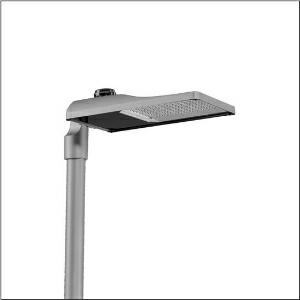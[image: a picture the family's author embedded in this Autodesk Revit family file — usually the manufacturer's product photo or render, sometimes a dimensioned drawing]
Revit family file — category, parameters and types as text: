
# Revit family: streetlight_sl_31_maxi___st1_5a_5xh8p7bn08sa_f059
name_source: partatom
category: Lighting Fixtures
units: mm (PartAtom-declared; Revit-internal decimal feet)

## family parameters
Cut with Voids When Loaded = No
Host = Face
Light Source = No
Part Type = Normal
Room Calculation Point = No
Round Connector Dimension = Use Diameter
Shared = No

## types (1)
- --- (1 x LED, 22010 lm, 208.6 W, 2200K)
    Apparent Load = 209 VA
    CIE Flux Codes = 22 53 95 100 100
    Color Rendering = 70
    Color Temperature = 2200K
    Default Elevation = 1800 mm
    Description = Streetlight SL 31 maxi NEMA (7pin) mast luminaire for post-top, side-entry; light control with lens of PMMA; light distribution: ST1.5a, direct asymmetric distribution, for standard-compliant lighting for roads and squares; LED: luminous flux: 22.010lm, light colour: 722, colour temperature: 2200K; luminous efficacy: 105,5lm/W; control: pre-setting: linear dimming characteristic, flexible luminous flux parameterisation, time-dependent luminous flux control, constant luminous flux control, intelligent temperature release in ECG and LED module, overheat protection; luminaire housing, of diecast aluminium, Siteco® metallic grey (DB 702S), corrosivity category C5 high according to DIN EN ISO 12944; cover of toughened safety glass, transparent, opened without tools; mast flange of diecast aluminium, Siteco® metallic grey (DB 702S), spigot size: 76/60mm, mast flange included unmounted; with cable H07RN-F 3x 1.5mm², cable length: 14,5m, connection cable pre-assembled; mains connection: 220..240V, AC, 50/60Hz; power consumption (at start of service life): 208,6W / (at end of service life): 233,1W / (with reduced operation 50%): 88W; protection rating (complete): IP66; insulation class (complete): insulation class I (protective earthing); impact resistance: IK10; certification: CE, ENEC, ENEC+, VDE, UKCA; permissible operating ambient temperature for outdoor applications: -40..+50°C; packaging unit: 1 piece

Light Distribution: ST1.5a
    Height = 79 mm
    Lamp = 1 x LED
    Lamp Light Flux = 22010 lm
    Lamp Power = 208.6 W
    Lamp count = 1
    Length = 657 mm
    Luminous efficacy = 106 lm/W
    Manufacturer = Siteco
    ModVariant = No
    Model = 5XH8P7BN08SA
    Number of Poles = 1
    OnlyDefault = Yes
    Power Factor = 1
    Product Name = Streetlight SL 31 maxi | ST1.5a
    Product group = mast luminaire | pylon top
    ProductGroupID = 6100
    Protection Class = Protection class I
    Protection Degree = IP 66
    RLX_Detail_Level = 1
    RLX_Emergency_Light_Flux = 0 lm
    RLX_Emergency_Type = 0
    RLX_Emergency_Type_DB = No
    RlxData = <blob elided: 30453 chars, md5=e5dbac57>
    Socket = socket
    Standby Power = 0 W
    System Light Flux = 22009 lm
    System Power = 209 W
    Type Comments = factory setting: luminous flux: 100 % | dim-lin: 254 | 718 mA
    Type Image = l_1300293.jpg
    URL = http://relux.com
    VarID = @adj_008253
    Voltage = 0 V
    Weight = 0.00 kg
    Width = 362 mm

## geometry (parser evidence)
native form markers: Blend x4, Sweep x11
no freeform markers — native parametric forms only
